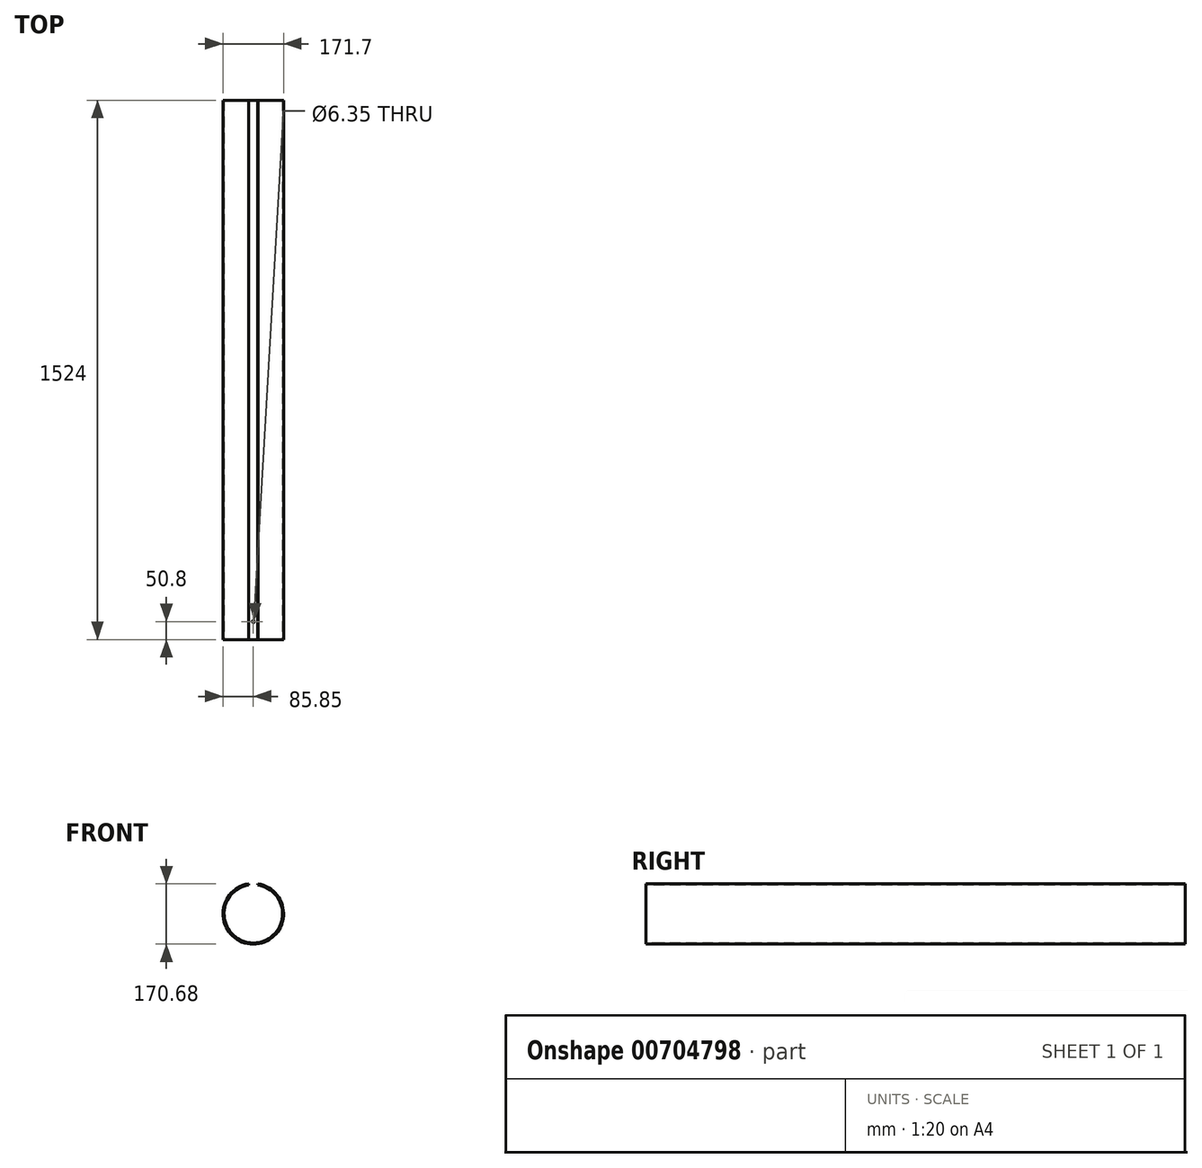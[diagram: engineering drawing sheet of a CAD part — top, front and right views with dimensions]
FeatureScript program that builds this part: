
annotation { "Feature Type Name" : "Feature", "Feature Type Description" : "" }
export const myFeature = defineFeature(function(context is Context, id is Id, definition is map)
    precondition{}
    {
        {
            var Q0;
            Q0=qCreatedBy(makeId("Front.planeOp"),FACE);
            var sketch = newSketch(context, id + "F0", { "sketchPlane" : qUnion([Q0])});
            skArc(sketch, "E0", {"start": v(-13.2, 84.83) * mm, "mid": v(0, -85.85) * mm, "end": v(13.2, 84.83) * mm});
            skArc(sketch, "E1", {"start": v(-12.7, 81.57) * mm, "mid": v(0, -82.55) * mm, "end": v(12.7, 81.57) * mm});
            skLineSegment(sketch, "E2", {"start": v(12.7, 81.57) * mm, "end": v(13.2, 84.83) * mm});
            skLineSegment(sketch, "E3", {"start": v(-12.7, 81.57) * mm, "end": v(-13.2, 84.83) * mm});
            skPoint(sketch, "E4.orphan", {"position": v(0, 82.55) * mm});
            skSolve(sketch);
        }
        {
            var Q0;
            Q0 = qSketchRegion(id + "F0", true);
            extrude(context, id + "F1", {"entities" : qUnion([Q0]), "oppositeDirection" : true, "depth" : 1524 * mm, "offsetDistance" : 25.4 * mm});
        }
        {
            var Q0;
            Q0=qCreatedBy(makeId("Top.planeOp"),FACE);
            var sketch = newSketch(context, id + "F2", { "sketchPlane" : qUnion([Q0])});
            skCircle(sketch, "E5", {"center": v(0, 50.8) * mm, "radius": 3.18 * mm});
            skSolve(sketch);
        }
        {
            var Q0;
            Q0 = qSketchRegion(id + "F2", true);
            extrude(context, id + "F3", {"entities" : qUnion([Q0]), "operationType" : NewBodyOperationType.REMOVE, "endBound" : BoundingType.SYMMETRIC, "depth" : 762 * mm, "offsetDistance" : 25.4 * mm});
        }
    });
